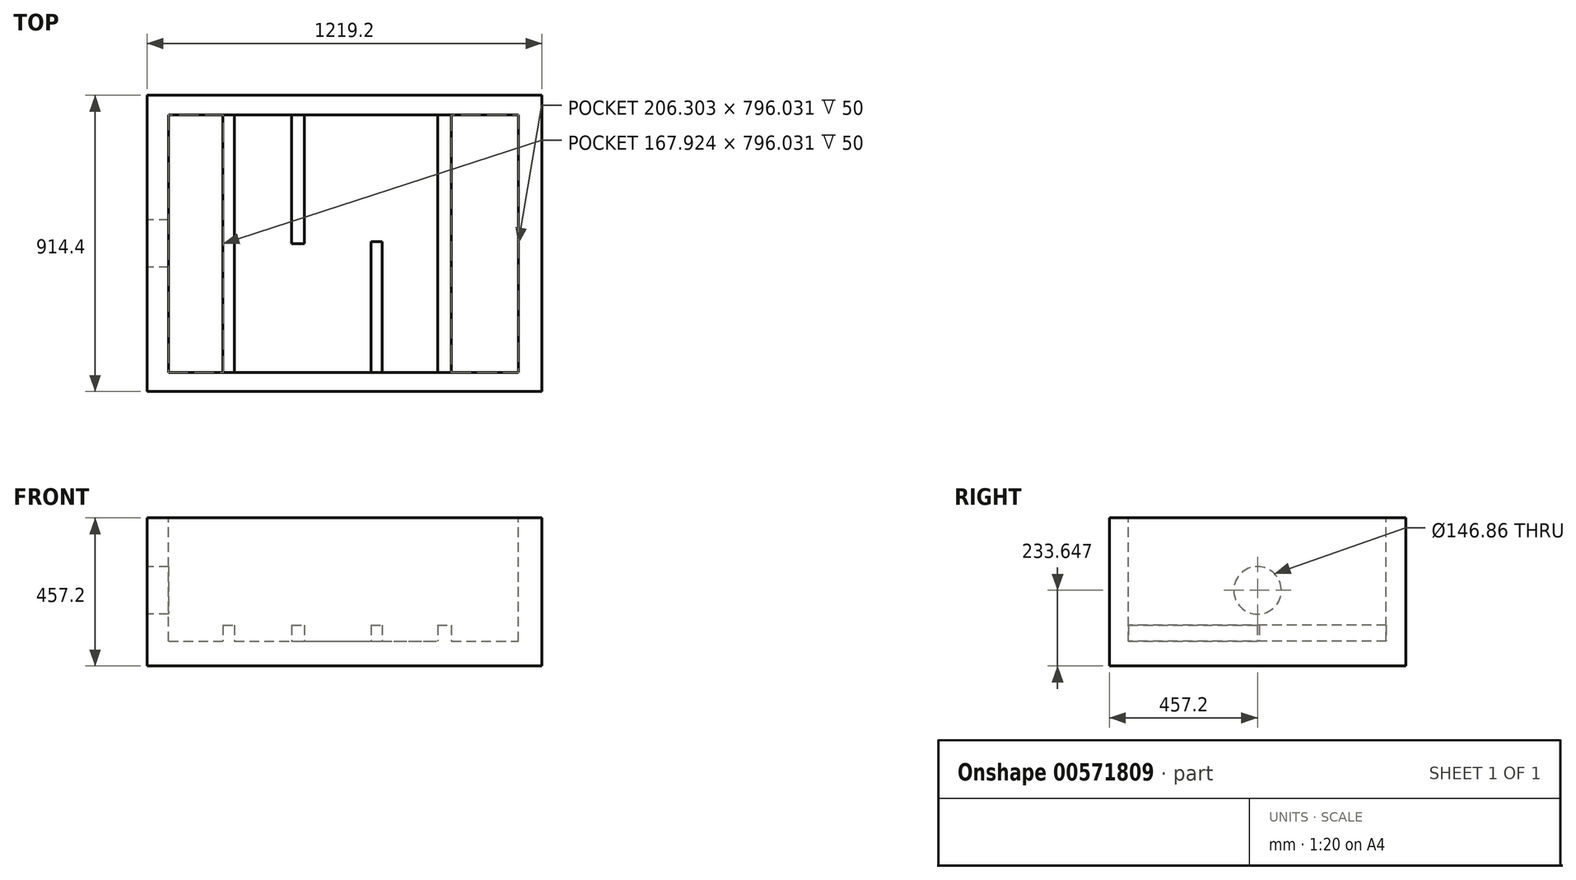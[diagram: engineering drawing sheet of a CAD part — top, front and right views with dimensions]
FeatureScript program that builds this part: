
annotation { "Feature Type Name" : "Feature", "Feature Type Description" : "" }
export const myFeature = defineFeature(function(context is Context, id is Id, definition is map)
    precondition{}
    {
        {
            var Q0;
            Q0=qCreatedBy(makeId("Top.planeOp"),FACE);
            var sketch = newSketch(context, id + "F0", { "sketchPlane" : qUnion([Q0])});
            skLineSegment(sketch, "E0.bottom", {"start": v(0, 0) * mm, "end": v(1219.2, 0) * mm});
            skLineSegment(sketch, "E0.top", {"start": v(0, -914.4) * mm, "end": v(1219.2, -914.4) * mm});
            skLineSegment(sketch, "E0.left", {"start": v(0, 0) * mm, "end": v(0, -914.4) * mm});
            skLineSegment(sketch, "E0.right", {"start": v(1219.2, 0) * mm, "end": v(1219.2, -914.4) * mm});
            skSolve(sketch);
        }
        {
            var Q0;
            Q0=makeQuery(id+"F0.imprint","IMPRINT",FACE,{"disambiguationData":[TD([[makeQuery(id+"F0.imprint","IMPRINT",EDGE,{"derivedFrom":sQuery(id+"F0.wireOp",EDGE,"E0.bottom")}),-1.0]])]});
            extrude(context, id + "F1", {"entities" : qUnion([Q0]), "depth" : 457.2 * mm, "offsetDistance" : 25 * mm});
        }
        {
            var Q0;
            Q0=makeQuery(id+"F1.opExtrude","CAP_FACE",FACE,{"disambiguationData":[OSD([sQuery(id+"F0.wireOp",EDGE,"E0.bottom"),sQuery(id+"F0.wireOp",EDGE,"E0.top"),sQuery(id+"F0.wireOp",EDGE,"E0.left"),sQuery(id+"F0.wireOp",EDGE,"E0.right")])],"isStart":false});
            var sketch = newSketch(context, id + "F2", { "sketchPlane" : qUnion([Q0])});
            skLineSegment(sketch, "E1.bottom", {"start": v(67, -60.07) * mm, "end": v(1145.89, -60.07) * mm});
            skLineSegment(sketch, "E1.top", {"start": v(67, -856.1) * mm, "end": v(1145.89, -856.1) * mm});
            skLineSegment(sketch, "E1.left", {"start": v(67, -60.07) * mm, "end": v(67, -856.1) * mm});
            skLineSegment(sketch, "E1.right", {"start": v(1145.89, -60.07) * mm, "end": v(1145.89, -856.1) * mm});
            skSolve(sketch);
        }
        {
            var Q0;
            Q0=makeQuery(id+"F2.imprint","IMPRINT",FACE,{"disambiguationData":[TD([[makeQuery(id+"F2.imprint","IMPRINT",EDGE,{"derivedFrom":sQuery(id+"F2.wireOp",EDGE,"E1.bottom")}),-1.0]])]});
            extrude(context, id + "F3", {"entities" : qUnion([Q0]), "operationType" : NewBodyOperationType.REMOVE, "oppositeDirection" : true, "depth" : 381 * mm, "offsetDistance" : 25 * mm});
        }
        {
            var Q0;
            Q0=makeQuery(id+"FT5yoBz6adEVe7U_1.boolean.opBoolean","MERGE",FACE,{"derivedFrom":[makeQuery(id+"FDOemP3XC8BuTrb_1.boolean.opBoolean","MERGE",FACE,{"derivedFrom":[makeQuery(id+"F1.opExtrude","SWEPT_FACE",FACE,{"disambiguationData":[OSD([sQuery(id+"F0.wireOp",EDGE,"E0.left")])]}),makeQuery(id+"FDOemP3XC8BuTrb_1.opExtrude","SWEPT_FACE",FACE,{"disambiguationData":[OSD([sQuery(id+"FvbdU1J3WiOg5tY_1.wireOp",EDGE,"7fbc68aa-e2c4-40a1-8e83-10def0eae923.left")])]})]}),makeQuery(id+"FT5yoBz6adEVe7U_1.opExtrude","SWEPT_FACE",FACE,{"disambiguationData":[OSD([sQuery(id+"FkQ7MoonNNGe5PK_1.wireOp",EDGE,"78f64100-6638-42ae-b00f-268d241173af.right")])]})]});
            var sketch = newSketch(context, id + "F4", { "sketchPlane" : qUnion([Q0])});
            skCircle(sketch, "E2", {"center": v(457.2, 233.65) * mm, "radius": 73.43 * mm});
            skPoint(sketch, "E2.centerSnap0", {"position": v(457.2, 457.2) * mm});
            skSolve(sketch);
        }
        {
            var Q0;
            Q0 = qSketchRegion(id + "F4", true);
            extrude(context, id + "F5", {"entities" : qUnion([Q0]), "operationType" : NewBodyOperationType.REMOVE, "oppositeDirection" : true, "depth" : 127 * mm, "offsetDistance" : 25 * mm});
        }
        {
            var Q0;
            Q0=makeQuery(id+"F3.boolean.opBoolean","COPY",FACE,{"derivedFrom":makeQuery(id+"F3.opExtrude","CAP_FACE",FACE,{"disambiguationData":[OSD([sQuery(id+"F2.wireOp",EDGE,"E1.bottom"),sQuery(id+"F2.wireOp",EDGE,"E1.top"),sQuery(id+"F2.wireOp",EDGE,"E1.left"),sQuery(id+"F2.wireOp",EDGE,"E1.right")])],"isStart":false})});
            var sketch = newSketch(context, id + "F6", { "sketchPlane" : qUnion([Q0])});
            skLineSegment(sketch, "E3.bottom", {"start": v(234.93, -60.07) * mm, "end": v(270.37, -60.07) * mm});
            skLineSegment(sketch, "E3.top", {"start": v(234.93, -856.1) * mm, "end": v(270.37, -856.1) * mm});
            skLineSegment(sketch, "E3.left", {"start": v(234.93, -60.07) * mm, "end": v(234.93, -856.1) * mm});
            skLineSegment(sketch, "E3.right", {"start": v(270.37, -60.07) * mm, "end": v(270.37, -856.1) * mm});
            skPoint(sketch, "E4.oppositeSnap0", {"position": v(270.37, -458.09) * mm});
            skLineSegment(sketch, "E4.bottom", {"start": v(446.8, -60.07) * mm, "end": v(485.33, -60.07) * mm});
            skLineSegment(sketch, "E4.top", {"start": v(446.8, -458.09) * mm, "end": v(485.33, -458.09) * mm});
            skLineSegment(sketch, "E4.left", {"start": v(446.8, -60.07) * mm, "end": v(446.8, -458.09) * mm});
            skLineSegment(sketch, "E4.right", {"start": v(485.33, -60.07) * mm, "end": v(485.33, -458.09) * mm});
            skLineSegment(sketch, "E5.bottom", {"start": v(691.3, -856.1) * mm, "end": v(725.94, -856.1) * mm});
            skLineSegment(sketch, "E5.top", {"start": v(691.3, -451.97) * mm, "end": v(725.94, -451.97) * mm});
            skLineSegment(sketch, "E5.left", {"start": v(691.3, -856.1) * mm, "end": v(691.3, -451.97) * mm});
            skLineSegment(sketch, "E5.right", {"start": v(725.94, -856.1) * mm, "end": v(725.94, -451.97) * mm});
            skLineSegment(sketch, "E6.bottom", {"start": v(896.77, -60.07) * mm, "end": v(939.59, -60.07) * mm});
            skLineSegment(sketch, "E6.top", {"start": v(896.77, -856.1) * mm, "end": v(939.59, -856.1) * mm});
            skLineSegment(sketch, "E6.left", {"start": v(896.77, -60.07) * mm, "end": v(896.77, -856.1) * mm});
            skLineSegment(sketch, "E6.right", {"start": v(939.59, -60.07) * mm, "end": v(939.59, -856.1) * mm});
            skSolve(sketch);
        }
        {
            var Q0;
            Q0=makeQuery(id+"F6.imprint","IMPRINT",FACE,{"disambiguationData":[TD([[makeQuery(id+"F6.imprint","IMPRINT",EDGE,{"derivedFrom":sQuery(id+"F6.wireOp",EDGE,"E4.bottom")}),-1.0]])]});
            var Q1;
            Q1=makeQuery(id+"F6.imprint","IMPRINT",FACE,{"disambiguationData":[TD([[makeQuery(id+"F6.imprint","IMPRINT",EDGE,{"derivedFrom":sQuery(id+"F6.wireOp",EDGE,"E5.bottom")}),1.0]])]});
            var Q2;
            Q2=makeQuery(id+"F6.imprint","IMPRINT",FACE,{"disambiguationData":[TD([[makeQuery(id+"F6.imprint","IMPRINT",EDGE,{"derivedFrom":sQuery(id+"F6.wireOp",EDGE,"E6.bottom")}),-1.0]])]});
            var Q3;
            Q3=makeQuery(id+"F6.imprint","IMPRINT",FACE,{"disambiguationData":[TD([[makeQuery(id+"F6.imprint","IMPRINT",EDGE,{"derivedFrom":sQuery(id+"F6.wireOp",EDGE,"E3.bottom")}),-1.0]])]});
            extrude(context, id + "F7", {"entities" : qUnion([Q0, Q1, Q2, Q3]), "operationType" : NewBodyOperationType.ADD, "depth" : 50 * mm, "offsetDistance" : 25 * mm});
        }
    });
